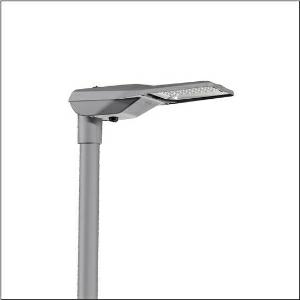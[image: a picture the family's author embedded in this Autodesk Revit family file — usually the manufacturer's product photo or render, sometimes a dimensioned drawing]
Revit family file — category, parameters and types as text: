
# Revit family: streetlight_sl_21_mini___p0_8ab_5xe2r33t08hb_4a65
name_source: partatom
category: Lighting Fixtures
units: mm (PartAtom-declared; Revit-internal decimal feet)

## family parameters
Cut with Voids When Loaded = No
Host = Face
Light Source = No
Part Type = Normal
Room Calculation Point = No
Round Connector Dimension = Use Diameter
Shared = No

## types (1)
- --- (1 x LED, 7850 lm, 66 W, 3000K)
    Apparent Load = 66 VA
    CIE Flux Codes = 36 71 98 100 100
    Color Rendering = 70
    Color Temperature = 3000K
    Default Elevation = 1800 mm
    Description = Streetlight SL 21 mini, mast luminaire, primary light control with lens, of PMMA, primary optical cover: cover, of toughened safety glass, transparent, light distribution: P0.8aB, light emission: direct distribution, primary light characteristic: asymmetric, installation type: post-top, side-entry, LED, High Power LED, rated luminous flux: 7.850lm, luminous efficacy: 119lm/W, light colour: 730, colour temperature: 3000K, control gear: D4i, control: pre-setting: logarithmic dimming characteristic, flexible luminous flux parameterisation, time-dependent luminous flux control, constant luminous flux control, overheat protection, mains connection: 220..240V, AC, 50/60Hz, start of lifetime: 66W, end of service life: 69W, reduction: 30W, luminaire housing, of diecast aluminium, powder-coated, Siteco® metallic grey (DB 702S), corrosivity category C5 mid according to DIN EN ISO 12944, multi-level sealing system, sealing non-destructively replaceable, inclination adjustable: 0°, 5°, 10°, 15°, please order mast flange separately, length: 628mm, width: 235mm, height: 110mm, mast flange for spigot size: 42mm (side-entry): 5XC10008XM4, 60/48mm (side-entry/post-top): 5XC10108XM2, 76/60mm (side-entry/post-top): 5XC10108XM1, mounting height: 4..8m, Smart Interface below and above, protection rating (complete): IP66, insulation class (complete): insulation class II (safety insulation), certification: CE, ENEC, ENEC+, VDE, impact resistance: IK09, permissible operating ambient temperature for outdoor applications: -40..+50°C, standard-compliant lighting for roads and squares, packaging unit: 1 piece

Light Distribution: P0.8aB
    Height = 110 mm
    Lamp = 1 x LED
    Lamp Light Flux = 7850 lm
    Lamp Power = 66 W
    Lamp count = 1
    Length = 625 mm
    Luminous efficacy = 119 lm/W
    Manufacturer = Siteco
    ModVariant = No
    Model = 5XE2R33T08HB
    Number of Poles = 1
    OnlyDefault = Yes
    Power Factor = 1
    Product Name = Streetlight SL 21 mini | P0.8aB
    Product group = mast luminaire | pylon top
    ProductGroupID = 6100
    Protection Class = Protection class II
    Protection Degree = IP 66
    RLX_Detail_Level = 1
    RLX_Emergency_Light_Flux = 0 lm
    RLX_Emergency_Type = 0
    RLX_Emergency_Type_DB = No
    RlxData = <blob elided: 93305 chars, md5=3eabbf35>
    Socket = socket
    Standby Power = 0 W
    System Light Flux = 7850 lm
    System Power = 66 W
    Type Comments = factory setting: luminous flux: 100 % | dim-lin: 254 | 670 mA
    Type Image = l_1003514.jpg
    URL = http://relux.com
    VarID = @adj_071936
    Voltage = 0 V
    Weight = 0.00 kg
    Width = 234 mm

## geometry (parser evidence)
native form markers: Blend x4, Sweep x11
no freeform markers — native parametric forms only
